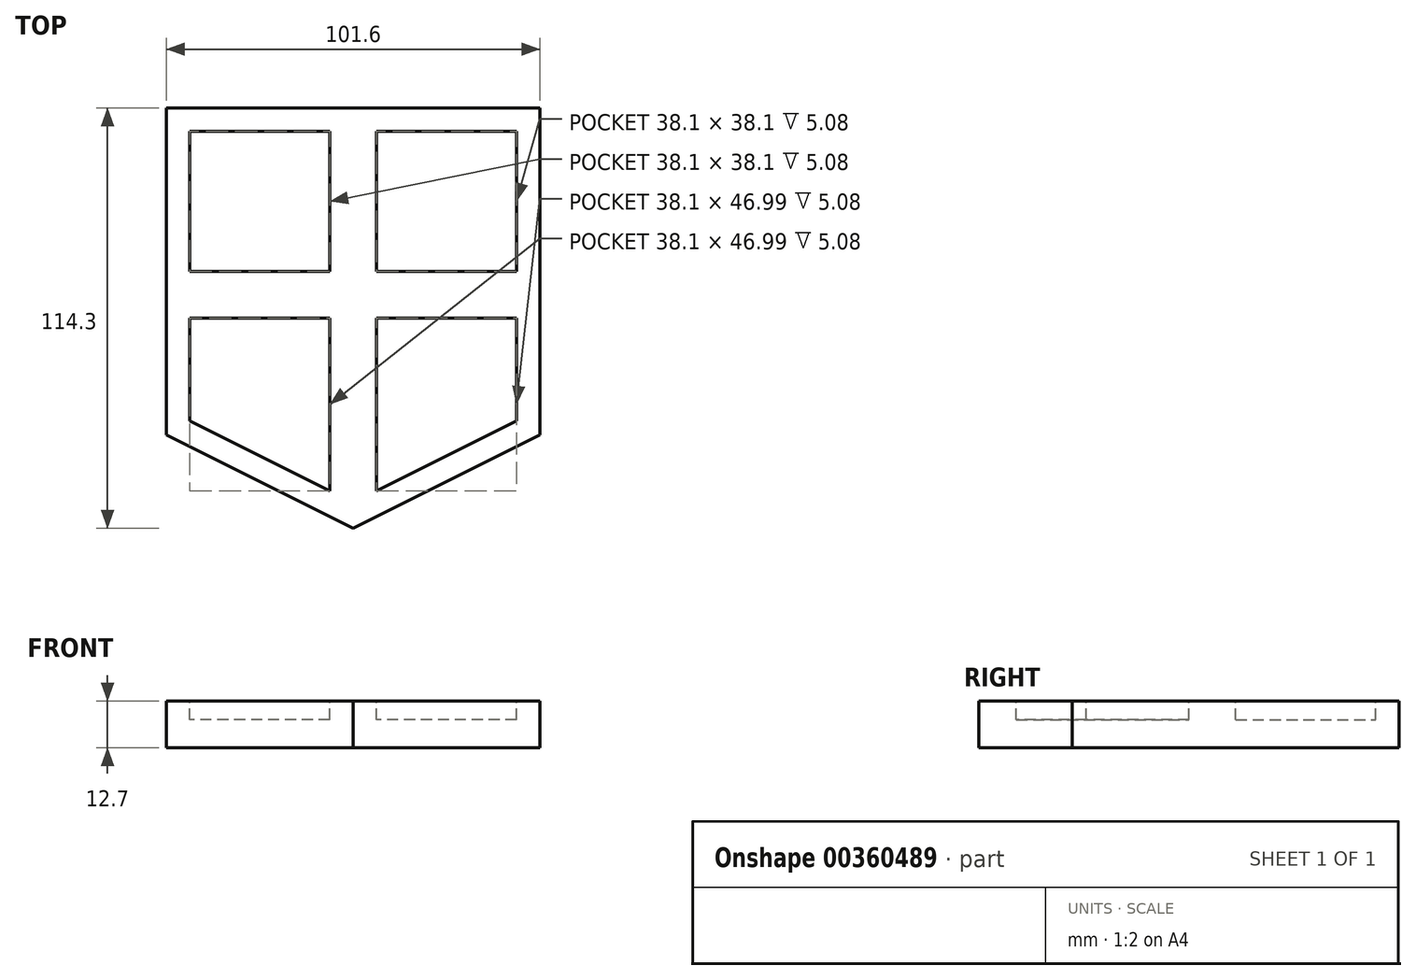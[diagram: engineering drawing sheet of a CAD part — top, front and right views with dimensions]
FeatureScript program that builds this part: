
annotation { "Feature Type Name" : "Feature", "Feature Type Description" : "" }
export const myFeature = defineFeature(function(context is Context, id is Id, definition is map)
    precondition{}
    {
        {
            var Q0;
            Q0=qCreatedBy(makeId("Top.planeOp"),FACE);
            var sketch = newSketch(context, id + "F0", { "sketchPlane" : qUnion([Q0])});
            skLineSegment(sketch, "E0", {"start": v(0, 0) * mm, "end": v(0, 50.8) * mm});
            skLineSegment(sketch, "E1", {"start": v(0, 50.8) * mm, "end": v(50.8, 50.8) * mm});
            skLineSegment(sketch, "E2", {"start": v(50.8, 50.8) * mm, "end": v(50.8, 0) * mm});
            skLineSegment(sketch, "E3", {"start": v(50.8, 0) * mm, "end": v(0, 0) * mm});
            skLineSegment(sketch, "E4", {"start": v(50.8, 0) * mm, "end": v(50.8, -38.1) * mm});
            skLineSegment(sketch, "E5", {"start": v(50.8, -38.1) * mm, "end": v(0, -63.5) * mm});
            skLineSegment(sketch, "E6", {"start": v(0, -63.5) * mm, "end": v(-50.8, -38.1) * mm});
            skLineSegment(sketch, "E7", {"start": v(-50.8, -38.1) * mm, "end": v(-50.8, 0) * mm});
            skLineSegment(sketch, "E8", {"start": v(-50.8, 0) * mm, "end": v(0, 0) * mm});
            skLineSegment(sketch, "E9", {"start": v(0, 50.8) * mm, "end": v(-50.8, 50.8) * mm});
            skLineSegment(sketch, "E10", {"start": v(-50.8, 50.8) * mm, "end": v(-50.8, 0) * mm});
            skLineSegment(sketch, "E11", {"start": v(0, 0) * mm, "end": v(0, -63.5) * mm});
            skSolve(sketch);
        }
        {
            var Q0;
            Q0=makeQuery(id+"F0.imprint","IMPRINT",FACE,{"disambiguationData":[TD([[makeQuery(id+"F0.imprint","IMPRINT",EDGE,{"derivedFrom":sQuery(id+"F0.wireOp",EDGE,"E0")}),1.0]])]});
            var Q1;
            Q1=makeQuery(id+"F0.imprint","IMPRINT",FACE,{"disambiguationData":[TD([[makeQuery(id+"F0.imprint","IMPRINT",EDGE,{"derivedFrom":sQuery(id+"F0.wireOp",EDGE,"E0")}),-1.0]])]});
            var Q2;
            Q2=makeQuery(id+"F0.imprint","IMPRINT",FACE,{"disambiguationData":[TD([[makeQuery(id+"F0.imprint","IMPRINT",EDGE,{"derivedFrom":sQuery(id+"F0.wireOp",EDGE,"E3")}),1.0]])]});
            var Q3;
            Q3=makeQuery(id+"F0.imprint","IMPRINT",FACE,{"disambiguationData":[TD([[makeQuery(id+"F0.imprint","IMPRINT",EDGE,{"derivedFrom":sQuery(id+"F0.wireOp",EDGE,"E6")}),-1.0]])]});
            extrude(context, id + "F1", {"entities" : qUnion([Q0, Q1, Q2, Q3]), "depth" : 12.7 * mm});
        }
        {
            var Q0;
            Q0=makeQuery(id+"F1.opExtrude","CAP_FACE",FACE,{"disambiguationData":[OSD([sQuery(id+"F0.wireOp",EDGE,"E1"),sQuery(id+"F0.wireOp",EDGE,"E2"),sQuery(id+"F0.wireOp",EDGE,"E4"),sQuery(id+"F0.wireOp",EDGE,"E5"),sQuery(id+"F0.wireOp",EDGE,"E6"),sQuery(id+"F0.wireOp",EDGE,"E7"),sQuery(id+"F0.wireOp",EDGE,"E9"),sQuery(id+"F0.wireOp",EDGE,"E10")])],"isStart":false});
            var sketch = newSketch(context, id + "F2", { "sketchPlane" : qUnion([Q0])});
            skLineSegment(sketch, "E12", {"start": v(-44.45, 44.45) * mm, "end": v(-44.45, 6.35) * mm});
            skLineSegment(sketch, "E13", {"start": v(-44.45, 6.35) * mm, "end": v(-6.35, 6.35) * mm});
            skLineSegment(sketch, "E14", {"start": v(-6.35, 6.35) * mm, "end": v(-6.35, 44.45) * mm});
            skLineSegment(sketch, "E15", {"start": v(-6.35, 44.45) * mm, "end": v(-44.45, 44.45) * mm});
            skLineSegment(sketch, "E16.MirrorCS", {"start": v(6.35, 6.35) * mm, "end": v(6.35, 44.45) * mm});
            skLineSegment(sketch, "E17.MirrorCS", {"start": v(6.35, 44.45) * mm, "end": v(44.45, 44.45) * mm});
            skLineSegment(sketch, "E18.MirrorCS", {"start": v(44.45, 44.45) * mm, "end": v(44.45, 6.35) * mm});
            skLineSegment(sketch, "E19.MirrorCS", {"start": v(44.45, 6.35) * mm, "end": v(6.35, 6.35) * mm});
            skSolve(sketch);
        }
        {
            var Q0;
            Q0=makeQuery(id+"F2.imprint","IMPRINT",FACE,{"disambiguationData":[TD([[makeQuery(id+"F2.imprint","IMPRINT",EDGE,{"derivedFrom":sQuery(id+"F2.wireOp",EDGE,"E12")}),-1.0]])]});
            var sketch = newSketch(context, id + "F3", { "sketchPlane" : qUnion([Q0])});
            skLineSegment(sketch, "E20", {"start": v(-44.45, -6.35) * mm, "end": v(-44.45, -34.3) * mm});
            skLineSegment(sketch, "E21", {"start": v(-44.45, -34.3) * mm, "end": v(-6.35, -53.34) * mm});
            skLineSegment(sketch, "E22", {"start": v(-6.35, -53.34) * mm, "end": v(-6.35, -6.35) * mm});
            skLineSegment(sketch, "E23", {"start": v(-6.35, -6.35) * mm, "end": v(-44.45, -6.35) * mm});
            skLineSegment(sketch, "E24.MirrorCS", {"start": v(6.35, -53.34) * mm, "end": v(6.35, -6.35) * mm});
            skLineSegment(sketch, "E25.MirrorCS", {"start": v(6.35, -6.35) * mm, "end": v(44.45, -6.35) * mm});
            skLineSegment(sketch, "E26.MirrorCS", {"start": v(44.45, -6.35) * mm, "end": v(44.45, -34.3) * mm});
            skLineSegment(sketch, "E27.MirrorCS", {"start": v(44.45, -34.3) * mm, "end": v(6.35, -53.34) * mm});
            skSolve(sketch);
        }
        {
            var Q0;
            Q0=makeQuery(id+"F2.imprint","IMPRINT",FACE,{"disambiguationData":[TD([[makeQuery(id+"F2.imprint","IMPRINT",EDGE,{"derivedFrom":sQuery(id+"F2.wireOp",EDGE,"E12")}),1.0]])]});
            var Q1;
            Q1=makeQuery(id+"F2.imprint","IMPRINT",FACE,{"disambiguationData":[TD([[makeQuery(id+"F2.imprint","IMPRINT",EDGE,{"derivedFrom":sQuery(id+"F2.wireOp",EDGE,"E16.MirrorCS")}),-1.0]])]});
            extrude(context, id + "F4", {"entities" : qUnion([Q0, Q1]), "operationType" : NewBodyOperationType.REMOVE, "oppositeDirection" : true, "depth" : 5.08 * mm});
        }
        {
            var Q0;
            Q0 = qSketchRegion(id + "F3", true);
            extrude(context, id + "F5", {"entities" : qUnion([Q0]), "operationType" : NewBodyOperationType.REMOVE, "oppositeDirection" : true, "depth" : 5.08 * mm});
        }
    });
